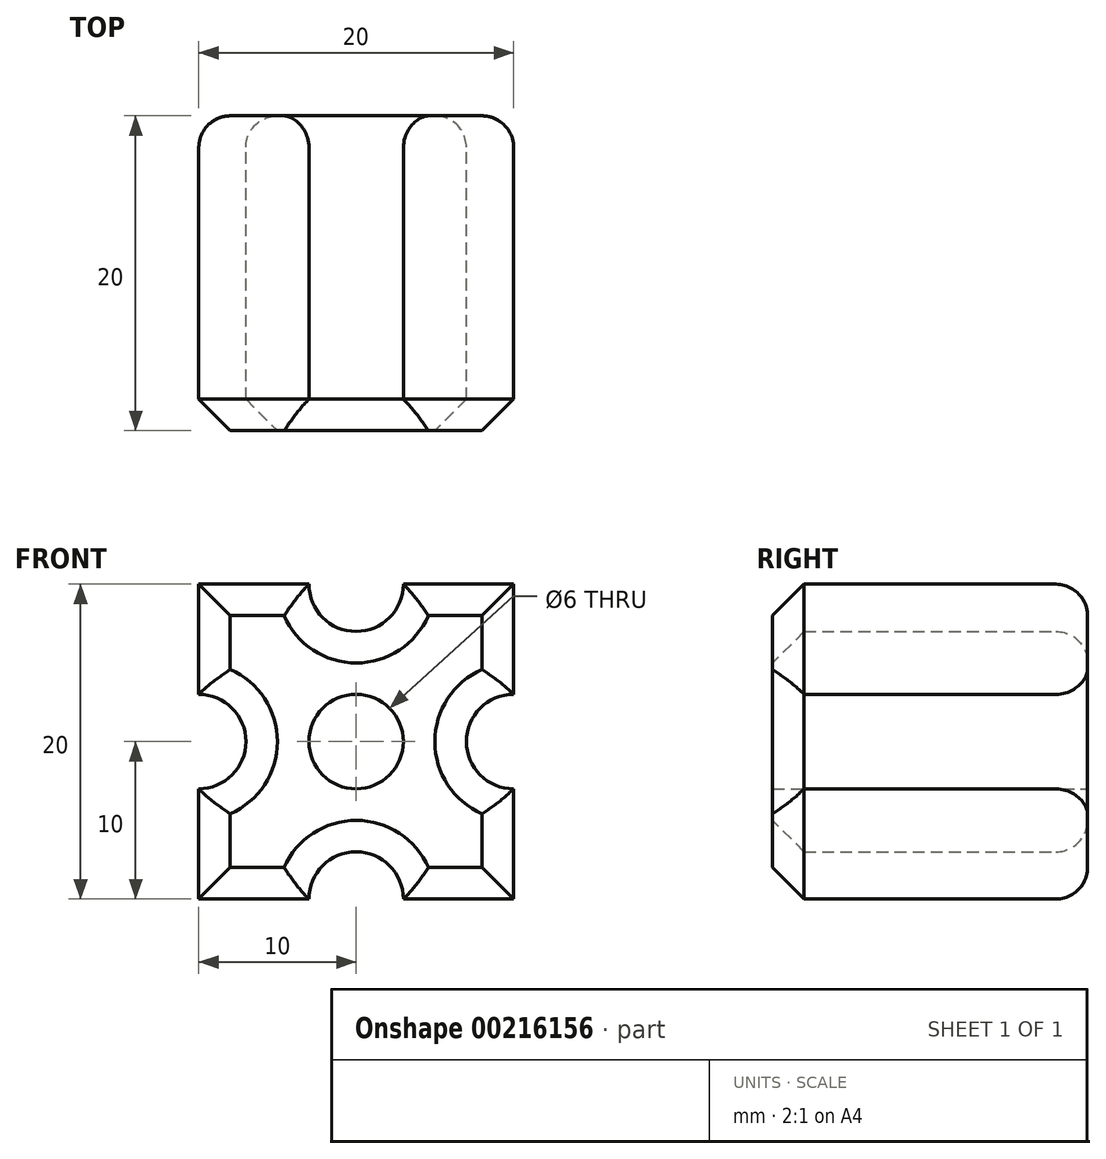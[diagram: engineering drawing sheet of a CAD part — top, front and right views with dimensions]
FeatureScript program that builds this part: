
annotation { "Feature Type Name" : "Feature", "Feature Type Description" : "" }
export const myFeature = defineFeature(function(context is Context, id is Id, definition is map)
    precondition{}
    {
        {
            var Q0;
            Q0=qCreatedBy(makeId("Front.planeOp"),FACE);
            var sketch = newSketch(context, id + "F0", { "sketchPlane" : qUnion([Q0])});
            skLineSegment(sketch, "E0.bottom", {"start": v(0, 0) * mm, "end": v(-20, 0) * mm});
            skLineSegment(sketch, "E0.top", {"start": v(0, 20) * mm, "end": v(-20, 20) * mm});
            skLineSegment(sketch, "E0.left", {"start": v(0, 0) * mm, "end": v(0, 20) * mm});
            skLineSegment(sketch, "E0.right", {"start": v(-20, 0) * mm, "end": v(-20, 20) * mm});
            skCircle(sketch, "E1", {"center": v(-10, 10) * mm, "radius": 3 * mm});
            skLineSegment(sketch, "E2", {"start": v(-10, 10) * mm, "end": v(-10, 20) * mm});
            skLineSegment(sketch, "E3", {"start": v(-10, 20) * mm, "end": v(-10, 0) * mm});
            skLineSegment(sketch, "E4", {"start": v(-10, 10) * mm, "end": v(0, 10) * mm});
            skLineSegment(sketch, "E5", {"start": v(0, 10) * mm, "end": v(-20, 10) * mm});
            skArc(sketch, "E6", {"start": v(0, 13) * mm, "mid": v(-3, 10) * mm, "end": v(0, 7) * mm});
            skArc(sketch, "E7", {"start": v(-7, 0) * mm, "mid": v(-10, 3) * mm, "end": v(-13, 0) * mm});
            skArc(sketch, "E8", {"start": v(-20, 7) * mm, "mid": v(-17, 10) * mm, "end": v(-20, 13) * mm});
            skArc(sketch, "E9", {"start": v(-7, 20) * mm, "mid": v(-10, 17) * mm, "end": v(-13, 20) * mm});
            skSolve(sketch);
        }
        {
            var Q0;
            {var subQ7=sQuery(id+"F0.wireOp",EDGE,"E0.left");var subQ8=sQuery(id+"F0.wireOp",EDGE,"E0.bottom");var subQ9=makeQuery(id+"F0.imprint","INTERSECT",VERTEX,{"derivedFrom":[subQ8,subQ7]});Q0=makeQuery(id+"F0.imprint","IMPRINT",FACE,{"disambiguationData":[TD([[makeQuery(id+"F0.imprint","IMPRINT",EDGE,{"disambiguationData":[TD([[subQ9,-1.0]])],"derivedFrom":subQ8}),-1.0]])]});}
            var Q1;
            {var subQ5=sQuery(id+"F0.wireOp",EDGE,"E0.right");var subQ6=sQuery(id+"F0.wireOp",EDGE,"E0.bottom");var subQ7=makeQuery(id+"F0.imprint","INTERSECT",VERTEX,{"derivedFrom":[subQ6,subQ5]});Q1=makeQuery(id+"F0.imprint","IMPRINT",FACE,{"disambiguationData":[TD([[makeQuery(id+"F0.imprint","IMPRINT",EDGE,{"disambiguationData":[TD([[subQ7,1.0]])],"derivedFrom":subQ6}),-1.0]])]});}
            var Q2;
            {var subQ5=sQuery(id+"F0.wireOp",EDGE,"E0.left");var subQ6=sQuery(id+"F0.wireOp",EDGE,"E0.top");var subQ7=makeQuery(id+"F0.imprint","INTERSECT",VERTEX,{"derivedFrom":[subQ6,subQ5]});Q2=makeQuery(id+"F0.imprint","IMPRINT",FACE,{"disambiguationData":[TD([[makeQuery(id+"F0.imprint","IMPRINT",EDGE,{"disambiguationData":[TD([[subQ7,-1.0]])],"derivedFrom":subQ6}),1.0]])]});}
            var Q3;
            {var subQ6=sQuery(id+"F0.wireOp",EDGE,"E0.right");var subQ9=sQuery(id+"F0.wireOp",EDGE,"E0.top");var subQ10=makeQuery(id+"F0.imprint","INTERSECT",VERTEX,{"derivedFrom":[subQ9,subQ6]});Q3=makeQuery(id+"F0.imprint","IMPRINT",FACE,{"disambiguationData":[TD([[makeQuery(id+"F0.imprint","IMPRINT",EDGE,{"disambiguationData":[TD([[subQ10,1.0]])],"derivedFrom":subQ9}),1.0]])]});}
            extrude(context, id + "F1", {"entities" : qUnion([Q0, Q1, Q2, Q3]), "depth" : 20 * mm});
        }
        {
            var Q0;
            {var subQ0=sQuery(id+"F0.wireOp",EDGE,"E0.left");Q0=makeQuery(id+"F1.opExtrude","CAP_EDGE",EDGE,{"disambiguationData":[OSD([subQ0]),TDD([makeQuery(id+"F0.imprint","IMPRINT",EDGE,{"disambiguationData":[TD([[makeQuery(id+"F0.imprint","INTERSECT",VERTEX,{"derivedFrom":[sQuery(id+"F0.wireOp",EDGE,"E0.top"),subQ0]}),1.0]])],"derivedFrom":subQ0})])],"isStart":false});}
            var Q1;
            {var subQ0=sQuery(id+"F0.wireOp",EDGE,"E0.left");Q1=makeQuery(id+"F1.opExtrude","CAP_EDGE",EDGE,{"disambiguationData":[OSD([subQ0]),TDD([makeQuery(id+"F0.imprint","IMPRINT",EDGE,{"disambiguationData":[TD([[makeQuery(id+"F0.imprint","INTERSECT",VERTEX,{"derivedFrom":[sQuery(id+"F0.wireOp",EDGE,"E0.bottom"),subQ0]}),-1.0]])],"derivedFrom":subQ0})])],"isStart":false});}
            var Q2;
            {var subQ0=sQuery(id+"F0.wireOp",EDGE,"E0.bottom");Q2=makeQuery(id+"F1.opExtrude","CAP_EDGE",EDGE,{"disambiguationData":[OSD([subQ0]),TDD([makeQuery(id+"F0.imprint","IMPRINT",EDGE,{"disambiguationData":[TD([[makeQuery(id+"F0.imprint","INTERSECT",VERTEX,{"derivedFrom":[subQ0,sQuery(id+"F0.wireOp",EDGE,"E0.left")]}),-1.0]])],"derivedFrom":subQ0})])],"isStart":false});}
            var Q3;
            {var subQ0=sQuery(id+"F0.wireOp",EDGE,"E0.bottom");Q3=makeQuery(id+"F1.opExtrude","CAP_EDGE",EDGE,{"disambiguationData":[OSD([subQ0]),TDD([makeQuery(id+"F0.imprint","IMPRINT",EDGE,{"disambiguationData":[TD([[makeQuery(id+"F0.imprint","INTERSECT",VERTEX,{"derivedFrom":[subQ0,sQuery(id+"F0.wireOp",EDGE,"E0.right")]}),1.0]])],"derivedFrom":subQ0})])],"isStart":false});}
            var Q4;
            {var subQ0=sQuery(id+"F0.wireOp",EDGE,"E0.right");Q4=makeQuery(id+"F1.opExtrude","CAP_EDGE",EDGE,{"disambiguationData":[OSD([subQ0]),TDD([makeQuery(id+"F0.imprint","IMPRINT",EDGE,{"disambiguationData":[TD([[makeQuery(id+"F0.imprint","INTERSECT",VERTEX,{"derivedFrom":[sQuery(id+"F0.wireOp",EDGE,"E0.bottom"),subQ0]}),-1.0]])],"derivedFrom":subQ0})])],"isStart":false});}
            var Q5;
            {var subQ0=sQuery(id+"F0.wireOp",EDGE,"E0.right");Q5=makeQuery(id+"F1.opExtrude","CAP_EDGE",EDGE,{"disambiguationData":[OSD([subQ0]),TDD([makeQuery(id+"F0.imprint","IMPRINT",EDGE,{"disambiguationData":[TD([[makeQuery(id+"F0.imprint","INTERSECT",VERTEX,{"derivedFrom":[sQuery(id+"F0.wireOp",EDGE,"E0.top"),subQ0]}),1.0]])],"derivedFrom":subQ0})])],"isStart":false});}
            var Q6;
            {var subQ0=sQuery(id+"F0.wireOp",EDGE,"E0.top");Q6=makeQuery(id+"F1.opExtrude","CAP_EDGE",EDGE,{"disambiguationData":[OSD([subQ0]),TDD([makeQuery(id+"F0.imprint","IMPRINT",EDGE,{"disambiguationData":[TD([[makeQuery(id+"F0.imprint","INTERSECT",VERTEX,{"derivedFrom":[subQ0,sQuery(id+"F0.wireOp",EDGE,"E0.right")]}),1.0]])],"derivedFrom":subQ0})])],"isStart":false});}
            var Q7;
            {var subQ0=sQuery(id+"F0.wireOp",EDGE,"E0.top");Q7=makeQuery(id+"F1.opExtrude","CAP_EDGE",EDGE,{"disambiguationData":[OSD([subQ0]),TDD([makeQuery(id+"F0.imprint","IMPRINT",EDGE,{"disambiguationData":[TD([[makeQuery(id+"F0.imprint","INTERSECT",VERTEX,{"derivedFrom":[subQ0,sQuery(id+"F0.wireOp",EDGE,"E0.left")]}),-1.0]])],"derivedFrom":subQ0})])],"isStart":false});}
            var Q8;
            Q8=makeQuery(id+"F1.opExtrude","CAP_EDGE",EDGE,{"disambiguationData":[OSD([sQuery(id+"F0.wireOp",EDGE,"E7")])],"isStart":false});
            var Q9;
            Q9=makeQuery(id+"F1.opExtrude","CAP_EDGE",EDGE,{"disambiguationData":[OSD([sQuery(id+"F0.wireOp",EDGE,"E8")])],"isStart":false});
            var Q10;
            Q10=makeQuery(id+"F1.opExtrude","CAP_EDGE",EDGE,{"disambiguationData":[OSD([sQuery(id+"F0.wireOp",EDGE,"E6")])],"isStart":false});
            var Q11;
            Q11=makeQuery(id+"F1.opExtrude","CAP_EDGE",EDGE,{"disambiguationData":[OSD([sQuery(id+"F0.wireOp",EDGE,"E9")])],"isStart":false});
            chamfer(context, id + "F2", {"entities" : qUnion([Q0, Q1, Q2, Q3, Q4, Q5, Q6, Q7, Q8, Q9, Q10, Q11]), "width" : 2 * mm, "tangentPropagation" : true});
        }
        {
            var Q0;
            {var subQ0=sQuery(id+"F0.wireOp",EDGE,"E0.left");Q0=makeQuery(id+"F1.opExtrude","CAP_EDGE",EDGE,{"disambiguationData":[OSD([subQ0]),TDD([makeQuery(id+"F0.imprint","IMPRINT",EDGE,{"disambiguationData":[TD([[makeQuery(id+"F0.imprint","INTERSECT",VERTEX,{"derivedFrom":[sQuery(id+"F0.wireOp",EDGE,"E0.bottom"),subQ0]}),-1.0]])],"derivedFrom":subQ0})])],"isStart":true});}
            var Q1;
            {var subQ0=sQuery(id+"F0.wireOp",EDGE,"E0.left");Q1=makeQuery(id+"F1.opExtrude","CAP_EDGE",EDGE,{"disambiguationData":[OSD([subQ0]),TDD([makeQuery(id+"F0.imprint","IMPRINT",EDGE,{"disambiguationData":[TD([[makeQuery(id+"F0.imprint","INTERSECT",VERTEX,{"derivedFrom":[sQuery(id+"F0.wireOp",EDGE,"E0.top"),subQ0]}),1.0]])],"derivedFrom":subQ0})])],"isStart":true});}
            var Q2;
            Q2=makeQuery(id+"F1.opExtrude","CAP_EDGE",EDGE,{"disambiguationData":[OSD([sQuery(id+"F0.wireOp",EDGE,"E6")])],"isStart":true});
            var Q3;
            {var subQ0=sQuery(id+"F0.wireOp",EDGE,"E0.top");Q3=makeQuery(id+"F1.opExtrude","CAP_EDGE",EDGE,{"disambiguationData":[OSD([subQ0]),TDD([makeQuery(id+"F0.imprint","IMPRINT",EDGE,{"disambiguationData":[TD([[makeQuery(id+"F0.imprint","INTERSECT",VERTEX,{"derivedFrom":[subQ0,sQuery(id+"F0.wireOp",EDGE,"E0.left")]}),-1.0]])],"derivedFrom":subQ0})])],"isStart":true});}
            var Q4;
            Q4=makeQuery(id+"F1.opExtrude","CAP_EDGE",EDGE,{"disambiguationData":[OSD([sQuery(id+"F0.wireOp",EDGE,"E9")])],"isStart":true});
            var Q5;
            {var subQ0=sQuery(id+"F0.wireOp",EDGE,"E0.top");Q5=makeQuery(id+"F1.opExtrude","CAP_EDGE",EDGE,{"disambiguationData":[OSD([subQ0]),TDD([makeQuery(id+"F0.imprint","IMPRINT",EDGE,{"disambiguationData":[TD([[makeQuery(id+"F0.imprint","INTERSECT",VERTEX,{"derivedFrom":[subQ0,sQuery(id+"F0.wireOp",EDGE,"E0.right")]}),1.0]])],"derivedFrom":subQ0})])],"isStart":true});}
            var Q6;
            {var subQ0=sQuery(id+"F0.wireOp",EDGE,"E0.right");Q6=makeQuery(id+"F1.opExtrude","CAP_EDGE",EDGE,{"disambiguationData":[OSD([subQ0]),TDD([makeQuery(id+"F0.imprint","IMPRINT",EDGE,{"disambiguationData":[TD([[makeQuery(id+"F0.imprint","INTERSECT",VERTEX,{"derivedFrom":[sQuery(id+"F0.wireOp",EDGE,"E0.top"),subQ0]}),1.0]])],"derivedFrom":subQ0})])],"isStart":true});}
            var Q7;
            Q7=makeQuery(id+"F1.opExtrude","CAP_EDGE",EDGE,{"disambiguationData":[OSD([sQuery(id+"F0.wireOp",EDGE,"E8")])],"isStart":true});
            var Q8;
            {var subQ0=sQuery(id+"F0.wireOp",EDGE,"E0.right");Q8=makeQuery(id+"F1.opExtrude","CAP_EDGE",EDGE,{"disambiguationData":[OSD([subQ0]),TDD([makeQuery(id+"F0.imprint","IMPRINT",EDGE,{"disambiguationData":[TD([[makeQuery(id+"F0.imprint","INTERSECT",VERTEX,{"derivedFrom":[sQuery(id+"F0.wireOp",EDGE,"E0.bottom"),subQ0]}),-1.0]])],"derivedFrom":subQ0})])],"isStart":true});}
            var Q9;
            {var subQ0=sQuery(id+"F0.wireOp",EDGE,"E0.bottom");Q9=makeQuery(id+"F1.opExtrude","CAP_EDGE",EDGE,{"disambiguationData":[OSD([subQ0]),TDD([makeQuery(id+"F0.imprint","IMPRINT",EDGE,{"disambiguationData":[TD([[makeQuery(id+"F0.imprint","INTERSECT",VERTEX,{"derivedFrom":[subQ0,sQuery(id+"F0.wireOp",EDGE,"E0.right")]}),1.0]])],"derivedFrom":subQ0})])],"isStart":true});}
            var Q10;
            Q10=makeQuery(id+"F1.opExtrude","CAP_EDGE",EDGE,{"disambiguationData":[OSD([sQuery(id+"F0.wireOp",EDGE,"E7")])],"isStart":true});
            var Q11;
            {var subQ0=sQuery(id+"F0.wireOp",EDGE,"E0.bottom");Q11=makeQuery(id+"F1.opExtrude","CAP_EDGE",EDGE,{"disambiguationData":[OSD([subQ0]),TDD([makeQuery(id+"F0.imprint","IMPRINT",EDGE,{"disambiguationData":[TD([[makeQuery(id+"F0.imprint","INTERSECT",VERTEX,{"derivedFrom":[subQ0,sQuery(id+"F0.wireOp",EDGE,"E0.left")]}),-1.0]])],"derivedFrom":subQ0})])],"isStart":true});}
            fillet(context, id + "F3", {"entities" : qUnion([Q0, Q1, Q2, Q3, Q4, Q5, Q6, Q7, Q8, Q9, Q10, Q11]), "radius" : 2 * mm, "tangentPropagation" : true, "allowEdgeOverflow" : false});
        }
    });
